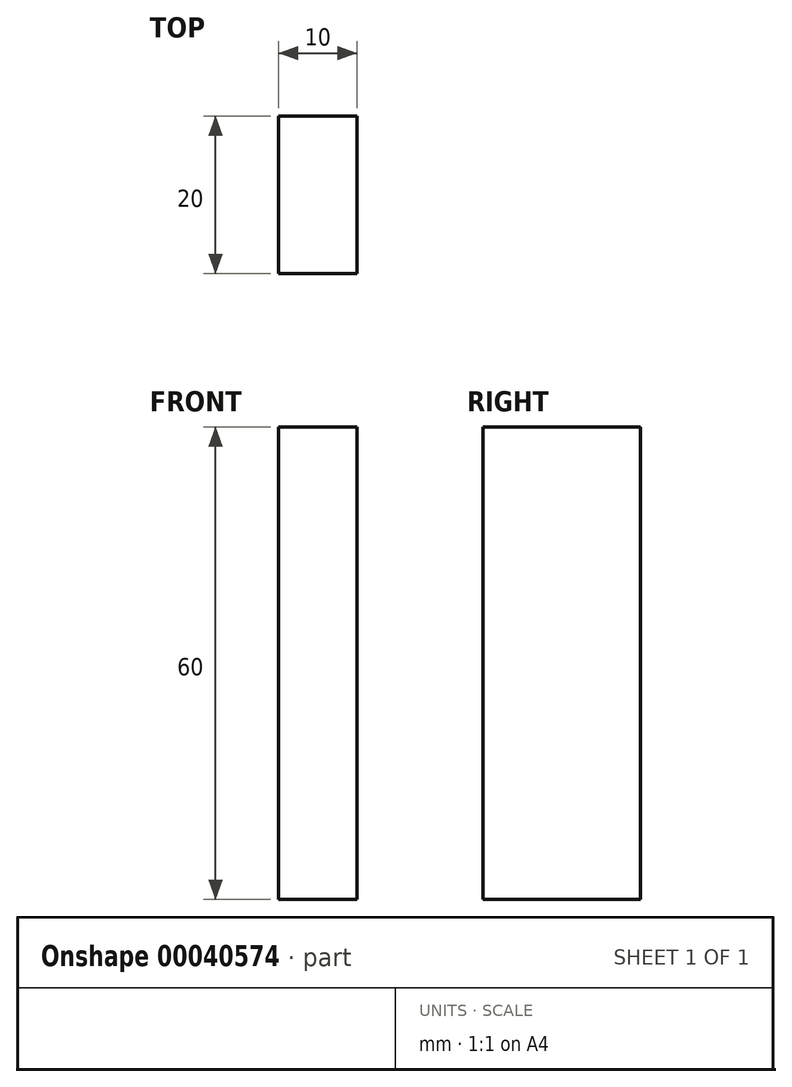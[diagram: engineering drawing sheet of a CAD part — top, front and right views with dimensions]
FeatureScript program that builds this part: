
annotation { "Feature Type Name" : "Feature", "Feature Type Description" : "" }
export const myFeature = defineFeature(function(context is Context, id is Id, definition is map)
    precondition{}
    {
        {
            var Q0;
            Q0=qCreatedBy(makeId("Top.planeOp"),FACE);
            var sketch = newSketch(context, id + "F0", { "sketchPlane" : qUnion([Q0])});
            skLineSegment(sketch, "E0.bottom", {"start": v(-21.71, -17) * mm, "end": v(-11.71, -17) * mm});
            skLineSegment(sketch, "E0.top", {"start": v(-21.71, 3) * mm, "end": v(-11.71, 3) * mm});
            skLineSegment(sketch, "E0.left", {"start": v(-21.71, -17) * mm, "end": v(-21.71, 3) * mm});
            skLineSegment(sketch, "E0.right", {"start": v(-11.71, -17) * mm, "end": v(-11.71, 3) * mm});
            skSolve(sketch);
        }
        {
            var Q0;
            Q0 = qSketchRegion(id + "F0", true);
            extrude(context, id + "F1", {"entities" : qUnion([Q0]), "depth" : 60 * mm});
        }
    });
